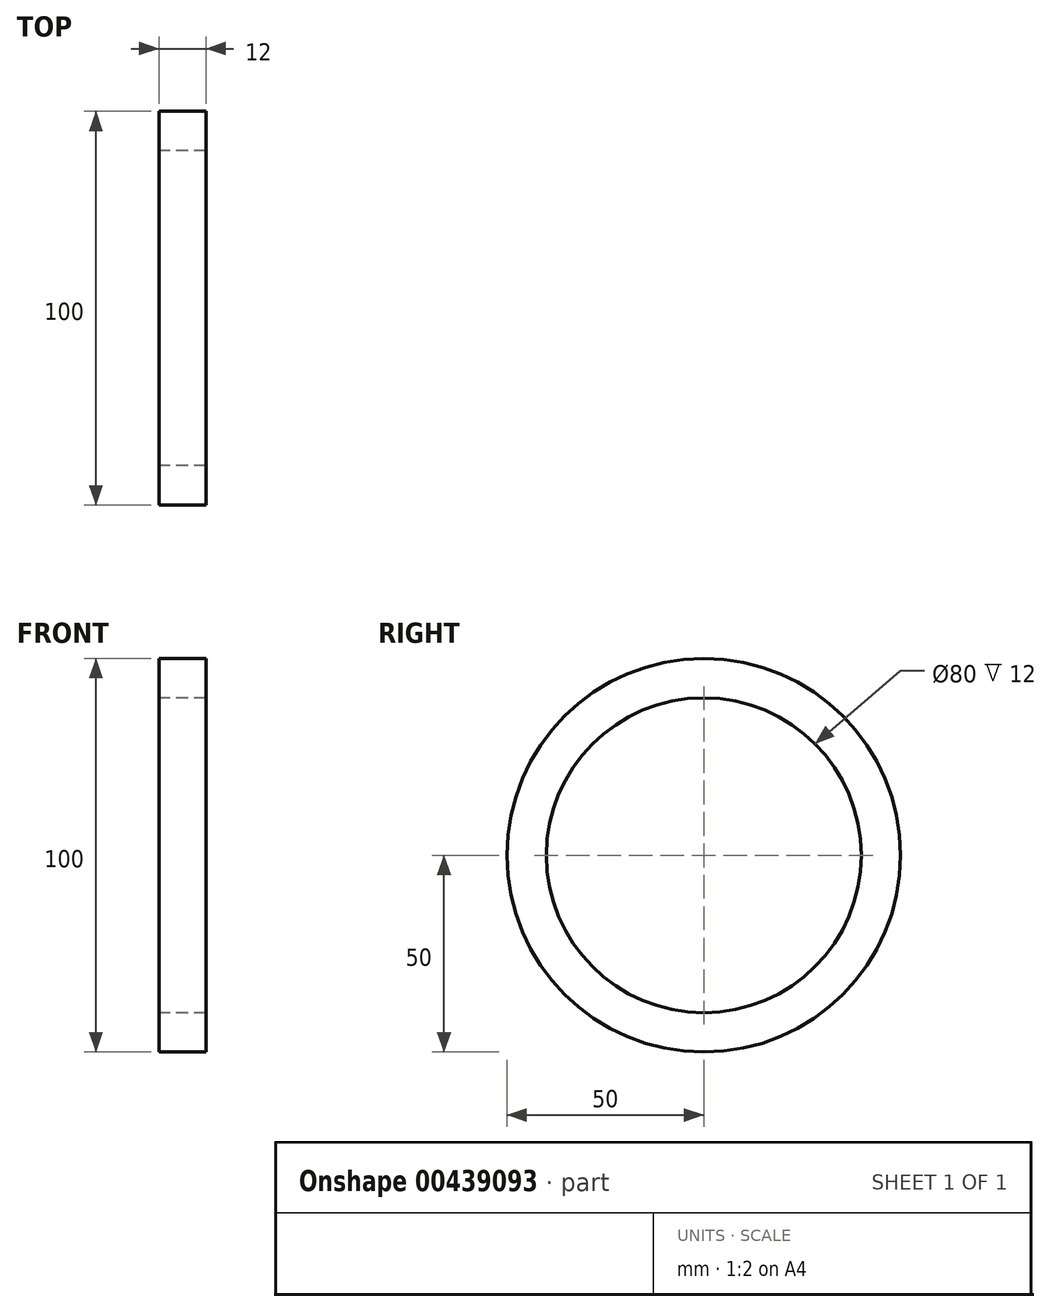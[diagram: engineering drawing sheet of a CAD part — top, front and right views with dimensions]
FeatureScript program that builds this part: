
annotation { "Feature Type Name" : "Feature", "Feature Type Description" : "" }
export const myFeature = defineFeature(function(context is Context, id is Id, definition is map)
    precondition{}
    {
        {
            var Q0;
            Q0=qCreatedBy(makeId("Right.planeOp"),FACE);
            var sketch = newSketch(context, id + "F0", { "sketchPlane" : qUnion([Q0])});
            skCircle(sketch, "E0", {"center": v(0, 0) * mm, "radius": 50 * mm});
            skCircle(sketch, "E1", {"center": v(0, 0) * mm, "radius": 40 * mm});
            skSolve(sketch);
        }
        {
            var Q0;
            Q0=qSketchRegion(id+"F0",true);
            extrude(context, id + "F1", {"entities" : qUnion([Q0]), "depth" : 12 * mm});
        }
    });
